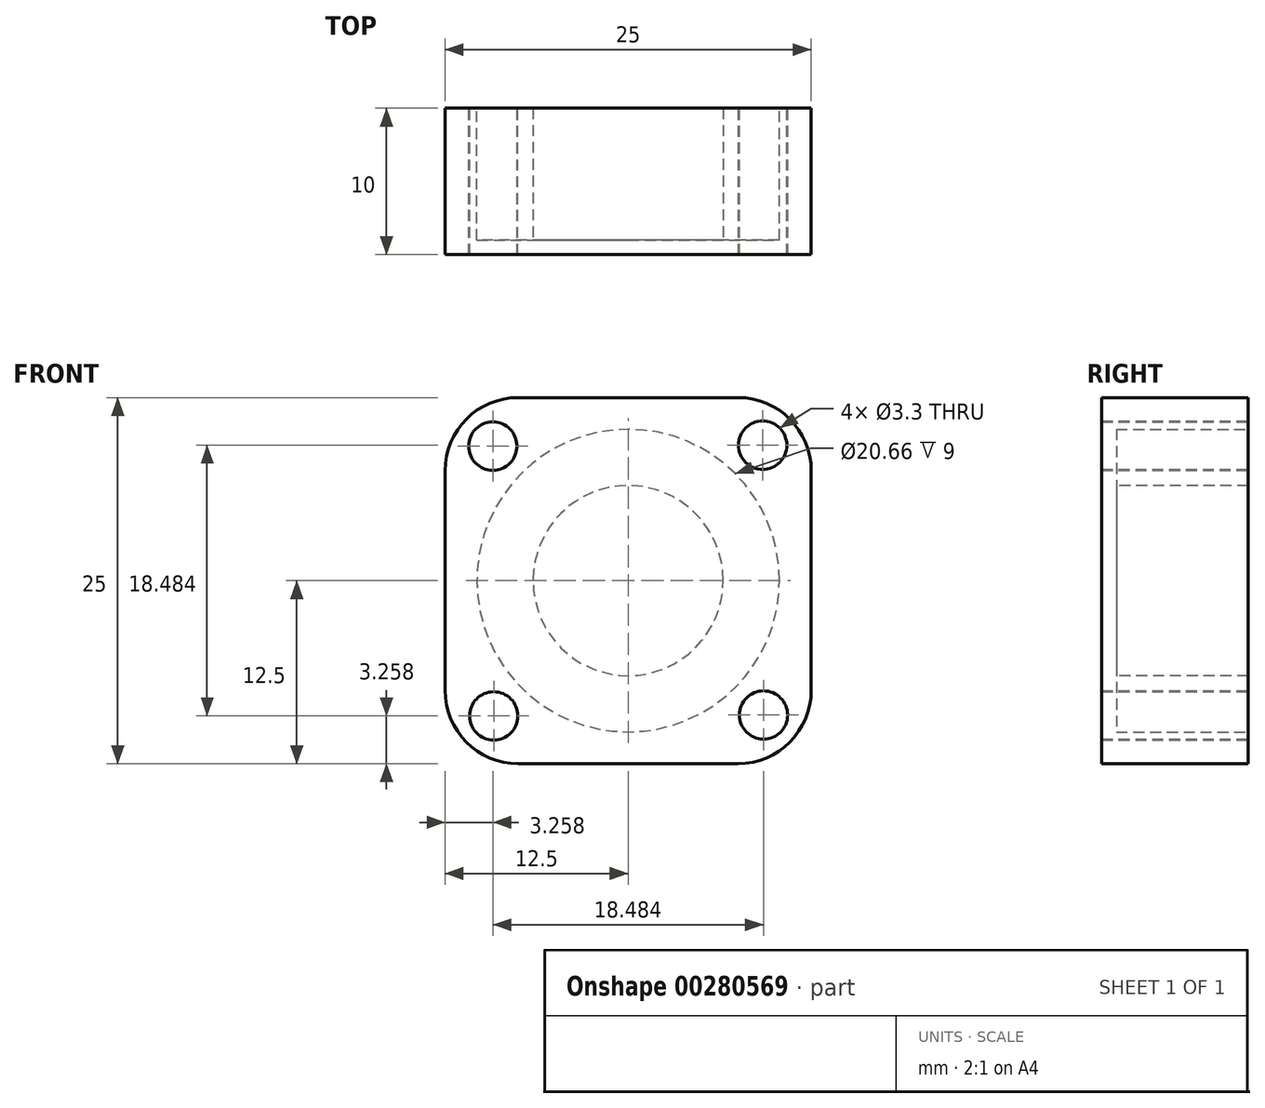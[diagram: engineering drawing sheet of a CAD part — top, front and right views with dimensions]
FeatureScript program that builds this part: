
annotation { "Feature Type Name" : "Feature", "Feature Type Description" : "" }
export const myFeature = defineFeature(function(context is Context, id is Id, definition is map)
    precondition{}
    {
        {
            var Q0;
            Q0=qCreatedBy(makeId("Front.planeOp"),FACE);
            var sketch = newSketch(context, id + "F0", { "sketchPlane" : qUnion([Q0])});
            skLineSegment(sketch, "E0.bottom", {"start": v(12.5, -12.5) * mm, "end": v(-12.5, -12.5) * mm});
            skLineSegment(sketch, "E0.top", {"start": v(12.5, 12.5) * mm, "end": v(-12.5, 12.5) * mm});
            skLineSegment(sketch, "E0.left", {"start": v(12.5, -12.5) * mm, "end": v(12.5, 12.5) * mm});
            skLineSegment(sketch, "E0.right", {"start": v(-12.5, -12.5) * mm, "end": v(-12.5, 12.5) * mm});
            skPoint(sketch, "E0.middle", {"position": v(0, 0) * mm});
            skSolve(sketch);
        }
        {
            var Q0;
            Q0=makeQuery(id+"F0.imprint","IMPRINT",FACE,{"disambiguationData":[TD([[makeQuery(id+"F0.imprint","IMPRINT",EDGE,{"derivedFrom":sQuery(id+"F0.wireOp",EDGE,"E0.bottom")}),-1.0]])]});
            extrude(context, id + "F1", {"entities" : qUnion([Q0]), "depth" : 10 * mm});
        }
        {
            var Q0;
            Q0=makeQuery(id+"F1.opExtrude","SWEPT_EDGE",EDGE,{"disambiguationData":[OSD([sQuery(id+"F0.wireOp",EDGE,"E0.top"),sQuery(id+"F0.wireOp",EDGE,"E0.left")])]});
            var Q1;
            Q1=makeQuery(id+"F1.opExtrude","SWEPT_EDGE",EDGE,{"disambiguationData":[OSD([sQuery(id+"F0.wireOp",EDGE,"E0.bottom"),sQuery(id+"F0.wireOp",EDGE,"E0.left")])]});
            var Q2;
            Q2=makeQuery(id+"F1.opExtrude","SWEPT_EDGE",EDGE,{"disambiguationData":[OSD([sQuery(id+"F0.wireOp",EDGE,"E0.top"),sQuery(id+"F0.wireOp",EDGE,"E0.right")])]});
            var Q3;
            Q3=makeQuery(id+"F1.opExtrude","SWEPT_EDGE",EDGE,{"disambiguationData":[OSD([sQuery(id+"F0.wireOp",EDGE,"E0.bottom"),sQuery(id+"F0.wireOp",EDGE,"E0.right")])]});
            fillet(context, id + "F2", {"entities" : qUnion([Q0, Q1, Q2, Q3]), "radius" : 5 * mm, "tangentPropagation" : true, "allowEdgeOverflow" : false});
        }
        {
            var Q0;
            Q0=makeQuery(id+"F1.opExtrude","CAP_FACE",FACE,{"disambiguationData":[OSD([sQuery(id+"F0.wireOp",EDGE,"E0.bottom"),sQuery(id+"F0.wireOp",EDGE,"E0.top"),sQuery(id+"F0.wireOp",EDGE,"E0.left"),sQuery(id+"F0.wireOp",EDGE,"E0.right")])],"isStart":true});
            var sketch = newSketch(context, id + "F3", { "sketchPlane" : qUnion([Q0])});
            skCircle(sketch, "E1", {"center": v(0, 0) * mm, "radius": 10.33 * mm});
            skSolve(sketch);
        }
        {
            var Q0;
            Q0 = qSketchRegion(id + "F3", true);
            extrude(context, id + "F4", {"entities" : qUnion([Q0]), "operationType" : NewBodyOperationType.REMOVE, "oppositeDirection" : true, "depth" : 9 * mm});
        }
        {
            var Q0;
            Q0=makeQuery(id+"F4.boolean.opBoolean","COPY",FACE,{"derivedFrom":makeQuery(id+"F4.opExtrude","CAP_FACE",FACE,{"disambiguationData":[OSD([sQuery(id+"F3.wireOp",EDGE,"E1")])],"isStart":false})});
            var sketch = newSketch(context, id + "F5", { "sketchPlane" : qUnion([Q0])});
            skCircle(sketch, "E2", {"center": v(0, 0) * mm, "radius": 6.49 * mm});
            skSolve(sketch);
        }
        {
            var Q0;
            Q0 = qSketchRegion(id + "F5", true);
            extrude(context, id + "F6", {"entities" : qUnion([Q0]), "operationType" : NewBodyOperationType.ADD, "depth" : 9 * mm});
        }
        {
            var Q0;
            Q0=makeQuery(id+"F1.opExtrude","CAP_FACE",FACE,{"disambiguationData":[OSD([sQuery(id+"F0.wireOp",EDGE,"E0.bottom"),sQuery(id+"F0.wireOp",EDGE,"E0.top"),sQuery(id+"F0.wireOp",EDGE,"E0.left"),sQuery(id+"F0.wireOp",EDGE,"E0.right")])],"isStart":true});
            var sketch = newSketch(context, id + "F7", { "sketchPlane" : qUnion([Q0])});
            skPoint(sketch, "E3", {"position": v(9.24, 9.18) * mm});
            skPoint(sketch, "E4.1.0", {"position": v(-9.18, 9.24) * mm});
            skPoint(sketch, "E4.2.0", {"position": v(-9.24, -9.18) * mm});
            skPoint(sketch, "E4.3.0", {"position": v(9.18, -9.24) * mm});
            skPoint(sketch, "E4.center", {"position": v(0, 0) * mm});
            skSolve(sketch);
        }
        {
            var Q0;
            Q0=sQuery(id+"F7.wireOp",VERTEX,"E3");
            var Q1;
            Q1=sQuery(id+"F7.wireOp",VERTEX,"E4.3.0");
            var Q2;
            Q2=sQuery(id+"F7.wireOp",VERTEX,"E4.2.0");
            var Q3;
            Q3=sQuery(id+"F7.wireOp",VERTEX,"E4.1.0");
            var Q4;
            Q4=makeQuery(id+"F1.opExtrude","SWEPT_BODY",BODY,{"disambiguationData":[OSD([sQuery(id+"F0.wireOp",EDGE,"E0.bottom"),sQuery(id+"F0.wireOp",EDGE,"E0.top"),sQuery(id+"F0.wireOp",EDGE,"E0.left"),sQuery(id+"F0.wireOp",EDGE,"E0.right")])]});
            hole(context, id + "F8", {"style" : HoleStyle.SIMPLE, "endStyle" : HoleEndStyle.THROUGH, "standardTappedOrClearance" : lookupTablePath({ "standard" : "ISO", "fit" : "Normal", "size" : "M3", "type" : "Clearance" }), "standardBlindInLast" : lookupTablePath({ "fit" : "Standard", "standard" : "ISO", "size" : "M3", "type" : "Clearance" }), "holeDiameter" : 3.3 * mm, "tappedDepth" : 12 * mm, "tapClearance" : 3, "locations" : qUnion([Q0, Q1, Q2, Q3]), "scope" : qUnion([Q4])});
        }
    });
